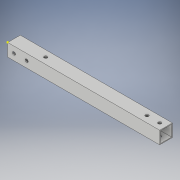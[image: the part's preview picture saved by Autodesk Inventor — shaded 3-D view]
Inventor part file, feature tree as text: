
AUTODESK INVENTOR PART (.ipt)
format: ipt  version: 2017 (Build 210142000, 142)  size: 125,952 bytes
history: native  units: in
note: dims shown in document units (in); Inventor stores cm internally (conversion verified against a paired STEP export)
features: sketch x4, extrude x3
ambient origin geometry x8: Origin, YZ Plane, XZ Plane, XY Plane, X Axis, Y Axis, Z Axis, Center Point
bodies: Solid1 (feature_tree)
feature tree (7):
  extrude  "Extrusion1"  Depth=1.0in
  extrude  "Extrusion2"  Depth=12.0in TaperAngle=0.0deg
  extrude  "Extrusion3"  Depth=0.5in
  sketch  "Sketch4"  dims[d7=1.0in d8=0.0in d9=1.5in d10=0.25in d11=0.5in d12=1.5in d13=1.0in d14=0.0in d15=2.5in]
  sketch  "Sketch1"  dims[d0=1.0in d1=1.0in]
  sketch  "Sketch2"  dims[d2=0.0625in d3=12.0in d4=0.0in]
  sketch  "Sketch3"  dims[d5=0.25in d6=0.5in]
